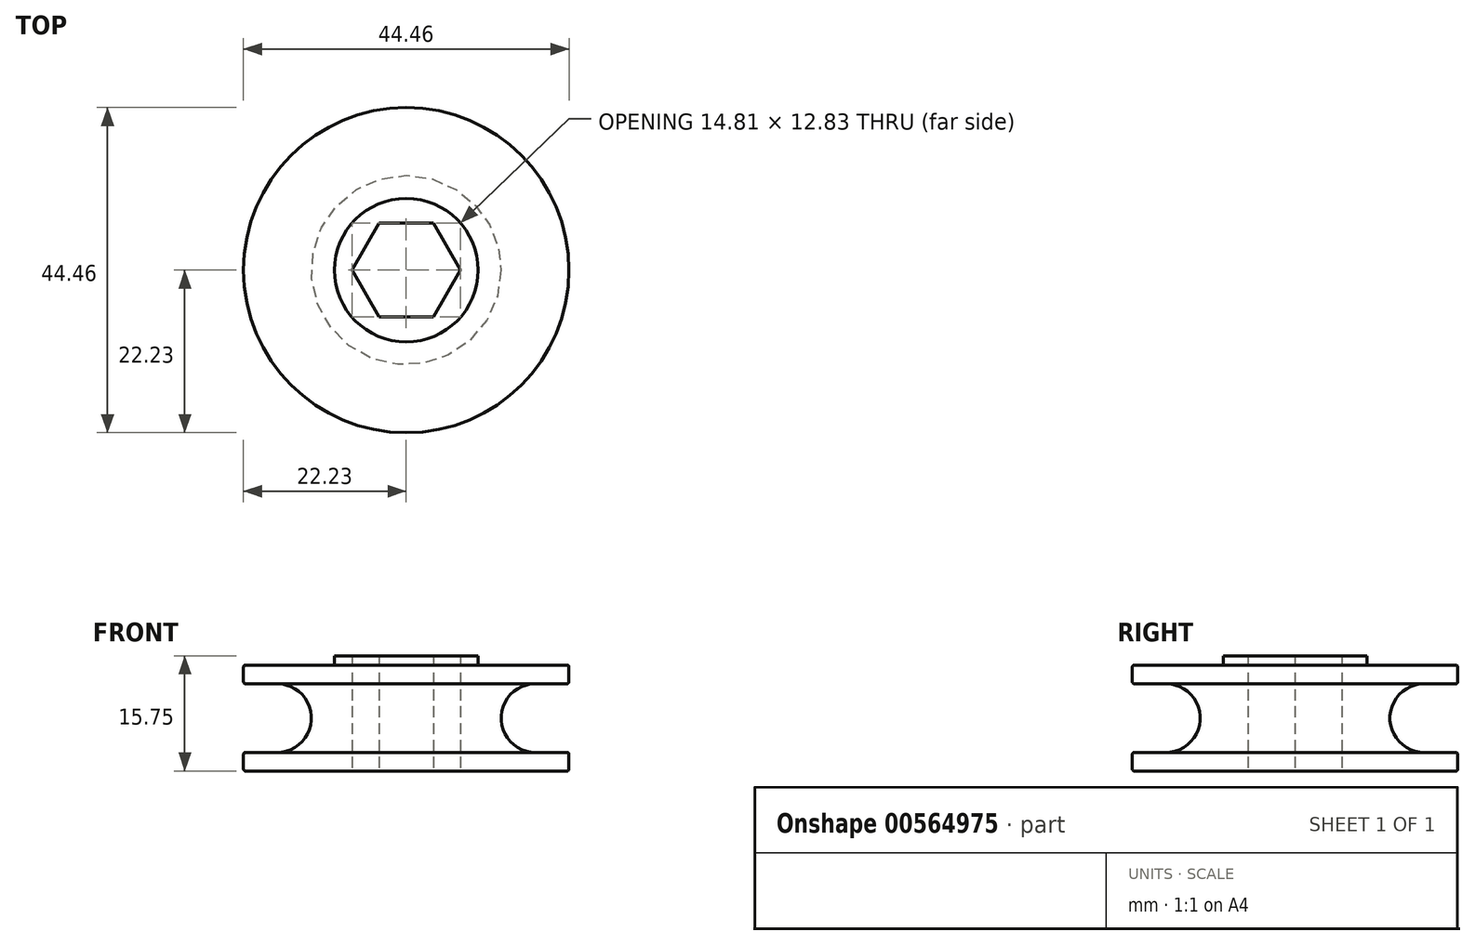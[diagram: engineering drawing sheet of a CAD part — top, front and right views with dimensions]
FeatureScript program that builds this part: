
annotation { "Feature Type Name" : "Feature", "Feature Type Description" : "" }
export const myFeature = defineFeature(function(context is Context, id is Id, definition is map)
    precondition{}
    {
        {
            var Q0;
            Q0=qCreatedBy(makeId("Top.planeOp"),FACE);
            var sketch = newSketch(context, id + "F0", { "sketchPlane" : qUnion([Q0])});
            skCircle(sketch, "E0", {"center": v(0, 0) * mm, "radius": 22.23 * mm});
            skCircle(sketch, "E1.cCircle", {"center": v(0, 0) * mm, "radius": 6.41 * mm, "construction": true});
            skLineSegment(sketch, "E1.0", {"start": v(-3.7, 6.41) * mm, "end": v(3.7, 6.41) * mm});
            skLineSegment(sketch, "E1.1", {"start": v(3.7, 6.41) * mm, "end": v(7.4, 0) * mm});
            skLineSegment(sketch, "E1.2", {"start": v(7.4, 0) * mm, "end": v(3.7, -6.41) * mm});
            skLineSegment(sketch, "E1.3", {"start": v(3.7, -6.41) * mm, "end": v(-3.7, -6.41) * mm});
            skLineSegment(sketch, "E1.4", {"start": v(-3.7, -6.41) * mm, "end": v(-7.4, 0) * mm});
            skLineSegment(sketch, "E1.5", {"start": v(-7.4, 0) * mm, "end": v(-3.7, 6.41) * mm});
            skPoint(sketch, "E1.0.midPoint", {"position": v(0, 6.41) * mm});
            skSolve(sketch);
        }
        {
            var Q0;
            Q0=makeQuery(id+"F0.imprint","IMPRINT",FACE,{"disambiguationData":[TD([[makeQuery(id+"F0.imprint","IMPRINT",EDGE,{"derivedFrom":sQuery(id+"F0.wireOp",EDGE,"E0")}),1.0]])]});
            extrude(context, id + "F1", {"entities" : qUnion([Q0]), "depth" : 14.48 * mm, "offsetDistance" : 25.4 * mm});
        }
        {
            var Q0;
            Q0=qCreatedBy(makeId("Front.planeOp"),FACE);
            var sketch = newSketch(context, id + "F2", { "sketchPlane" : qUnion([Q0])});
            skLineSegment(sketch, "E2.0", {"start": v(-7.4, 14.48) * mm, "end": v(-7.4, 0) * mm});
            skLineSegment(sketch, "E3", {"start": v(-22.23, 0) * mm, "end": v(-22.23, 14.48) * mm});
            skPoint(sketch, "E4", {"position": v(-22.23, 11.94) * mm});
            skPoint(sketch, "E5", {"position": v(-22.23, 2.54) * mm});
            skLineSegment(sketch, "E6", {"start": v(-22.23, 11.94) * mm, "end": v(-17.65, 11.94) * mm});
            skLineSegment(sketch, "E7", {"start": v(-22.23, 2.54) * mm, "end": v(-17.65, 2.54) * mm});
            skArc(sketch, "E8", {"start": v(-17.65, 2.54) * mm, "mid": v(-12.95, 7.24) * mm, "end": v(-17.65, 11.94) * mm});
            skLineSegment(sketch, "E9", {"start": v(-22.23, 11.94) * mm, "end": v(-22.23, 2.54) * mm});
            skSolve(sketch);
        }
        {
            var Q0;
            Q0 = qSketchRegion(id + "F2", true);
            var Q1;
            Q1=makeQuery(id+"F1.opExtrude","CAP_EDGE",EDGE,{"disambiguationData":[OSD([sQuery(id+"F0.wireOp",EDGE,"E0")])],"isStart":false});
            revolve(context, id + "F3", {"operationType" : NewBodyOperationType.REMOVE, "entities" : qUnion([Q0]), "axis" : qUnion([Q1]), "revolveType" : RevolveType.FULL, "oppositeDirection" : true});
        }
        {
            var Q0;
            Q0=makeQuery(id+"F1.opExtrude","CAP_FACE",FACE,{"disambiguationData":[OSD([sQuery(id+"F0.wireOp",EDGE,"E0"),sQuery(id+"F0.wireOp",EDGE,"E1.0"),sQuery(id+"F0.wireOp",EDGE,"E1.1"),sQuery(id+"F0.wireOp",EDGE,"E1.2"),sQuery(id+"F0.wireOp",EDGE,"E1.3"),sQuery(id+"F0.wireOp",EDGE,"E1.4"),sQuery(id+"F0.wireOp",EDGE,"E1.5")])],"isStart":false});
            var sketch = newSketch(context, id + "F4", { "sketchPlane" : qUnion([Q0])});
            skCircle(sketch, "E10.0.0", {"center": v(0, 0) * mm, "radius": 22.23 * mm});
            skLineSegment(sketch, "E11.0", {"start": v(3.7, 6.41) * mm, "end": v(7.4, 0) * mm});
            skLineSegment(sketch, "E12.0", {"start": v(-3.7, 6.41) * mm, "end": v(3.7, 6.41) * mm});
            skLineSegment(sketch, "E13.0", {"start": v(-7.4, 0) * mm, "end": v(-3.7, 6.41) * mm});
            skLineSegment(sketch, "E14.0", {"start": v(-3.7, -6.41) * mm, "end": v(-7.4, 0) * mm});
            skLineSegment(sketch, "E15.0", {"start": v(3.7, -6.41) * mm, "end": v(-3.7, -6.41) * mm});
            skLineSegment(sketch, "E16.0", {"start": v(7.4, 0) * mm, "end": v(3.7, -6.41) * mm});
            skCircle(sketch, "E17", {"center": v(0, 0) * mm, "radius": 9.8 * mm});
            skSolve(sketch);
        }
        {
            var Q0;
            Q0=makeQuery(id+"F4.imprint","IMPRINT",FACE,{"disambiguationData":[TD([[makeQuery(id+"F4.imprint","IMPRINT",EDGE,{"derivedFrom":sQuery(id+"F4.wireOp",EDGE,"E11.0")}),1.0]])]});
            extrude(context, id + "F5", {"entities" : qUnion([Q0]), "operationType" : NewBodyOperationType.ADD, "depth" : 1.27 * mm, "offsetDistance" : 25.4 * mm});
        }
        {
            var Q0;
            Q0=makeQuery(id+"F1.opExtrude","CAP_FACE",FACE,{"disambiguationData":[OSD([sQuery(id+"F0.wireOp",EDGE,"E0"),sQuery(id+"F0.wireOp",EDGE,"E1.0"),sQuery(id+"F0.wireOp",EDGE,"E1.1"),sQuery(id+"F0.wireOp",EDGE,"E1.2"),sQuery(id+"F0.wireOp",EDGE,"E1.3"),sQuery(id+"F0.wireOp",EDGE,"E1.4"),sQuery(id+"F0.wireOp",EDGE,"E1.5")])],"isStart":false});
            var Q1;
            Q1=makeQuery(id+"F1.opExtrude","CAP_FACE",FACE,{"disambiguationData":[OSD([sQuery(id+"F0.wireOp",EDGE,"E0"),sQuery(id+"F0.wireOp",EDGE,"E1.0"),sQuery(id+"F0.wireOp",EDGE,"E1.1"),sQuery(id+"F0.wireOp",EDGE,"E1.2"),sQuery(id+"F0.wireOp",EDGE,"E1.3"),sQuery(id+"F0.wireOp",EDGE,"E1.4"),sQuery(id+"F0.wireOp",EDGE,"E1.5")])],"isStart":true});
            cPlane(context, id + "F6", {"entities" : qUnion([Q0, Q1]), "cplaneType" : CPlaneType.MID_PLANE, "offset" : 25.4 * mm, "width" : 152.4 * mm, "height" : 152.4 * mm});
        }
        {
            var Q0;
            Q0=makeQuery(id+"F1.opExtrude","CAP_EDGE",EDGE,{"disambiguationData":[OSD([sQuery(id+"F0.wireOp",EDGE,"E0")])],"isStart":true});
            var Q1;
            Q1=makeQuery(id+"F1.opExtrude","CAP_EDGE",EDGE,{"disambiguationData":[OSD([sQuery(id+"F0.wireOp",EDGE,"E0")])],"isStart":false});
            var Q2;
            Q2=makeQuery(id+"F3.boolean.opBoolean","COPY",EDGE,{"derivedFrom":makeQuery(id+"F3.opRevolve","SWEPT_EDGE",EDGE,{"disambiguationData":[OSD([sQuery(id+"F2.wireOp",EDGE,"E6"),sQuery(id+"F2.wireOp",EDGE,"E9")])]})});
            var Q3;
            {var subQ0=sQuery(id+"F0.wireOp",EDGE,"E0");Q3=makeQuery(id+"F3.boolean.opBoolean","SPLIT",FACE,{"disambiguationData":[TD([makeQuery(id+"F3.opRevolve","SWEPT_FACE",FACE,{"disambiguationData":[OSD([sQuery(id+"F2.wireOp",EDGE,"E7")])]})])],"derivedFrom":makeQuery(id+"F1.opExtrude","SWEPT_FACE",FACE,{"disambiguationData":[OSD([subQ0])]})});}
            fillet(context, id + "F7", {"entities" : qUnion([Q0, Q1, Q2, Q3]), "radius" : 0.25 * mm, "tangentPropagation" : true, "allowEdgeOverflow" : false});
        }
    });
